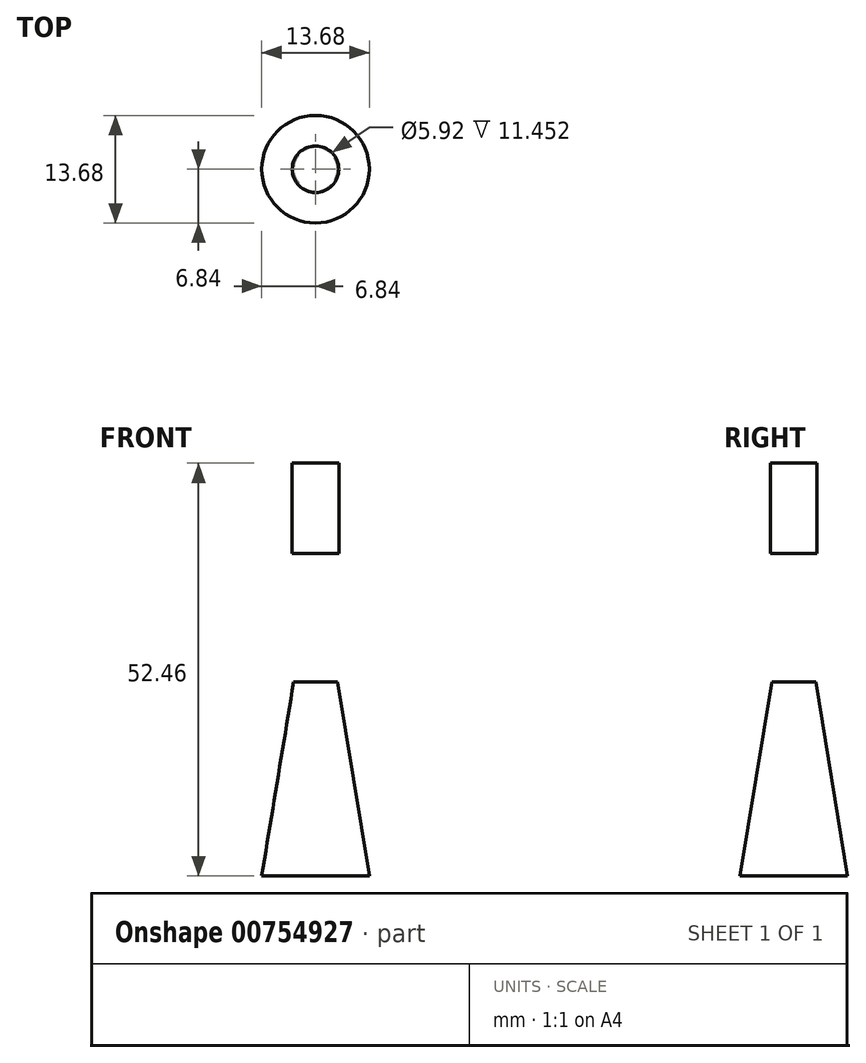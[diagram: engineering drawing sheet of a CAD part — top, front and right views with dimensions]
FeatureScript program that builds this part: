
annotation { "Feature Type Name" : "Feature", "Feature Type Description" : "" }
export const myFeature = defineFeature(function(context is Context, id is Id, definition is map)
    precondition{}
    {
        {
            var Q0;
            Q0=qCreatedBy(makeId("Front.planeOp"),FACE);
            var sketch = newSketch(context, id + "F0", { "sketchPlane" : qUnion([Q0])});
            skLineSegment(sketch, "E0", {"start": v(0, 24.65) * mm, "end": v(-2.78, 24.65) * mm});
            skLineSegment(sketch, "E1", {"start": v(-2.78, 24.65) * mm, "end": v(-6.84, 0) * mm});
            skLineSegment(sketch, "E2", {"start": v(-6.84, 0) * mm, "end": v(0, 0) * mm});
            skLineSegment(sketch, "E3", {"start": v(0, 30.05) * mm, "end": v(0, 0) * mm, "construction": true});
            skSolve(sketch);
        }
        {
            var Q0;
            Q0=sQuery(id+"F0.wireOp",EDGE,"E1");
            var Q1;
            Q1=sQuery(id+"F0.wireOp",EDGE,"E3");
            revolve(context, id + "F1", {"bodyType" : ToolBodyType.SURFACE, "surfaceOperationType" : NewSurfaceOperationType.NEW, "surfaceEntities" : qUnion([Q0]), "axis" : qUnion([Q1]), "revolveType" : RevolveType.FULL});
        }
        {
            var Q0;
            Q0=qCreatedBy(makeId("Front.planeOp"),FACE);
            var sketch = newSketch(context, id + "F2", { "sketchPlane" : qUnion([Q0])});
            skLineSegment(sketch, "E4", {"start": v(0, 52.46) * mm, "end": v(2.96, 52.46) * mm});
            skLineSegment(sketch, "E5", {"start": v(2.96, 52.46) * mm, "end": v(2.96, 41) * mm});
            skLineSegment(sketch, "E6", {"start": v(2.96, 41) * mm, "end": v(0, 41) * mm});
            skLineSegment(sketch, "E7", {"start": v(0, 55.52) * mm, "end": v(0, 36.1) * mm, "construction": true});
            skSolve(sketch);
        }
        {
            var Q0;
            Q0=sQuery(id+"F2.wireOp",EDGE,"E5");
            var Q1;
            Q1=sQuery(id+"F2.wireOp",EDGE,"E4");
            var Q2;
            Q2=sQuery(id+"F2.wireOp",EDGE,"E6");
            var Q3;
            Q3=sQuery(id+"F2.wireOp",EDGE,"E7");
            revolve(context, id + "F3", {"bodyType" : ToolBodyType.SURFACE, "surfaceOperationType" : NewSurfaceOperationType.NEW, "surfaceEntities" : qUnion([Q0, Q1, Q2]), "axis" : qUnion([Q3]), "revolveType" : RevolveType.FULL});
        }
    });
